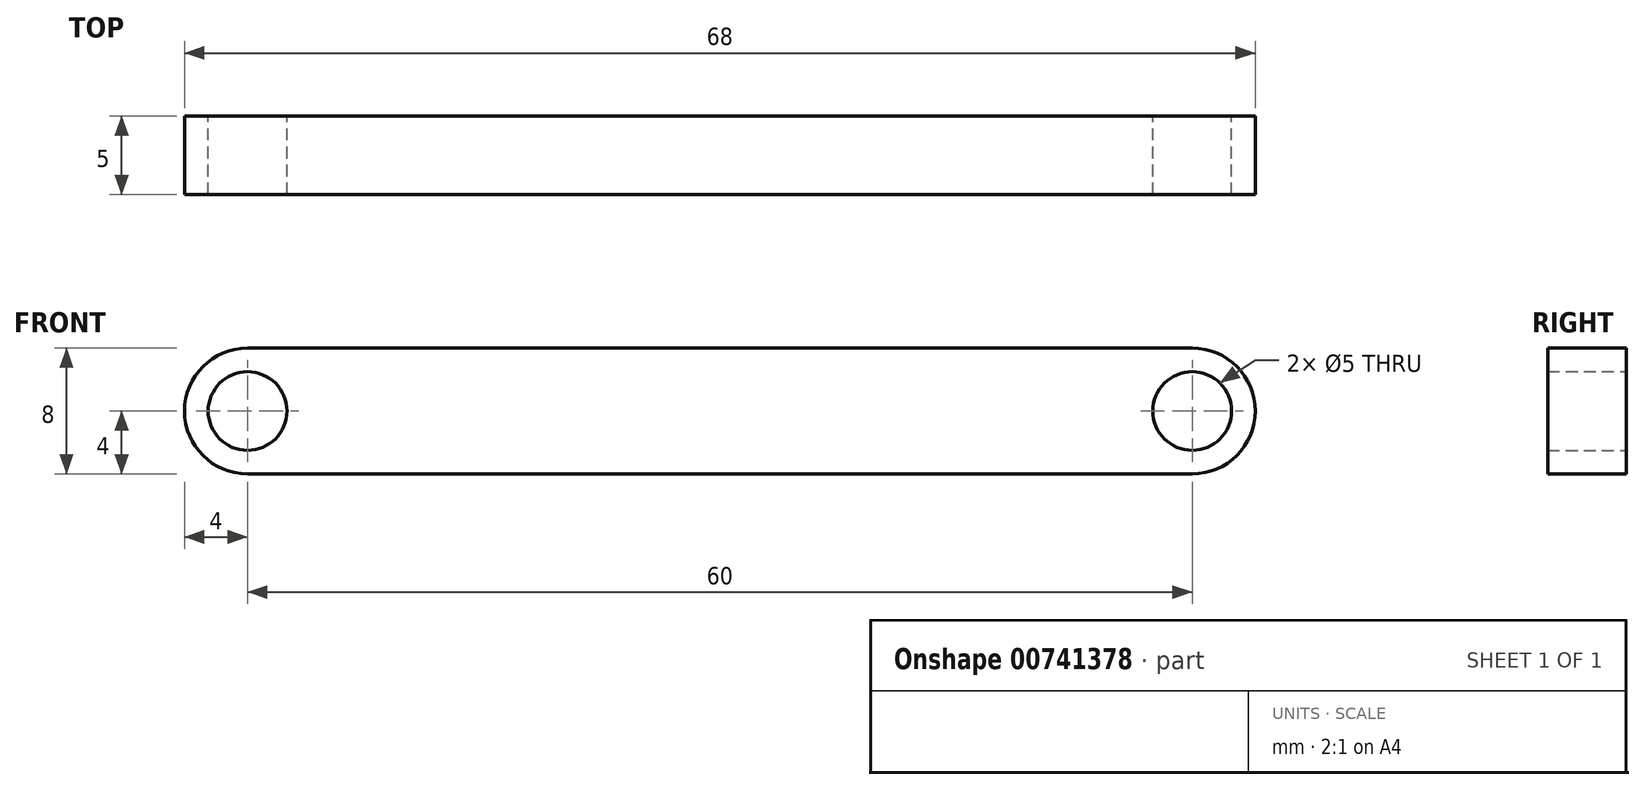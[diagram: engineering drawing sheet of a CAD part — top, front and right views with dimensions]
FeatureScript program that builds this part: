
annotation { "Feature Type Name" : "Feature", "Feature Type Description" : "" }
export const myFeature = defineFeature(function(context is Context, id is Id, definition is map)
    precondition{}
    {
        {
            var Q0;
            Q0=qCreatedBy(makeId("Front.planeOp"),FACE);
            var sketch = newSketch(context, id + "F0", { "sketchPlane" : qUnion([Q0])});
            skArc(sketch, "E0", {"start": v(0, 4) * mm, "mid": v(-4, 0) * mm, "end": v(0, -4) * mm});
            skArc(sketch, "E1", {"start": v(60, -4) * mm, "mid": v(64, 0) * mm, "end": v(60, 4) * mm});
            skLineSegment(sketch, "E2", {"start": v(0, 4) * mm, "end": v(60, 4) * mm});
            skLineSegment(sketch, "E3", {"start": v(0, -4) * mm, "end": v(60, -4) * mm});
            skCircle(sketch, "E4", {"center": v(0, 0) * mm, "radius": 2.5 * mm});
            skCircle(sketch, "E5", {"center": v(60, 0) * mm, "radius": 2.5 * mm});
            skSolve(sketch);
        }
        {
            var Q0;
            Q0=makeQuery(id+"F0.imprint","IMPRINT",FACE,{"disambiguationData":[TD([[makeQuery(id+"F0.imprint","IMPRINT",EDGE,{"derivedFrom":sQuery(id+"F0.wireOp",EDGE,"E0")}),1.0]])]});
            extrude(context, id + "F1", {"entities" : qUnion([Q0]), "depth" : 5 * mm, "offsetDistance" : 25 * mm});
        }
    });
